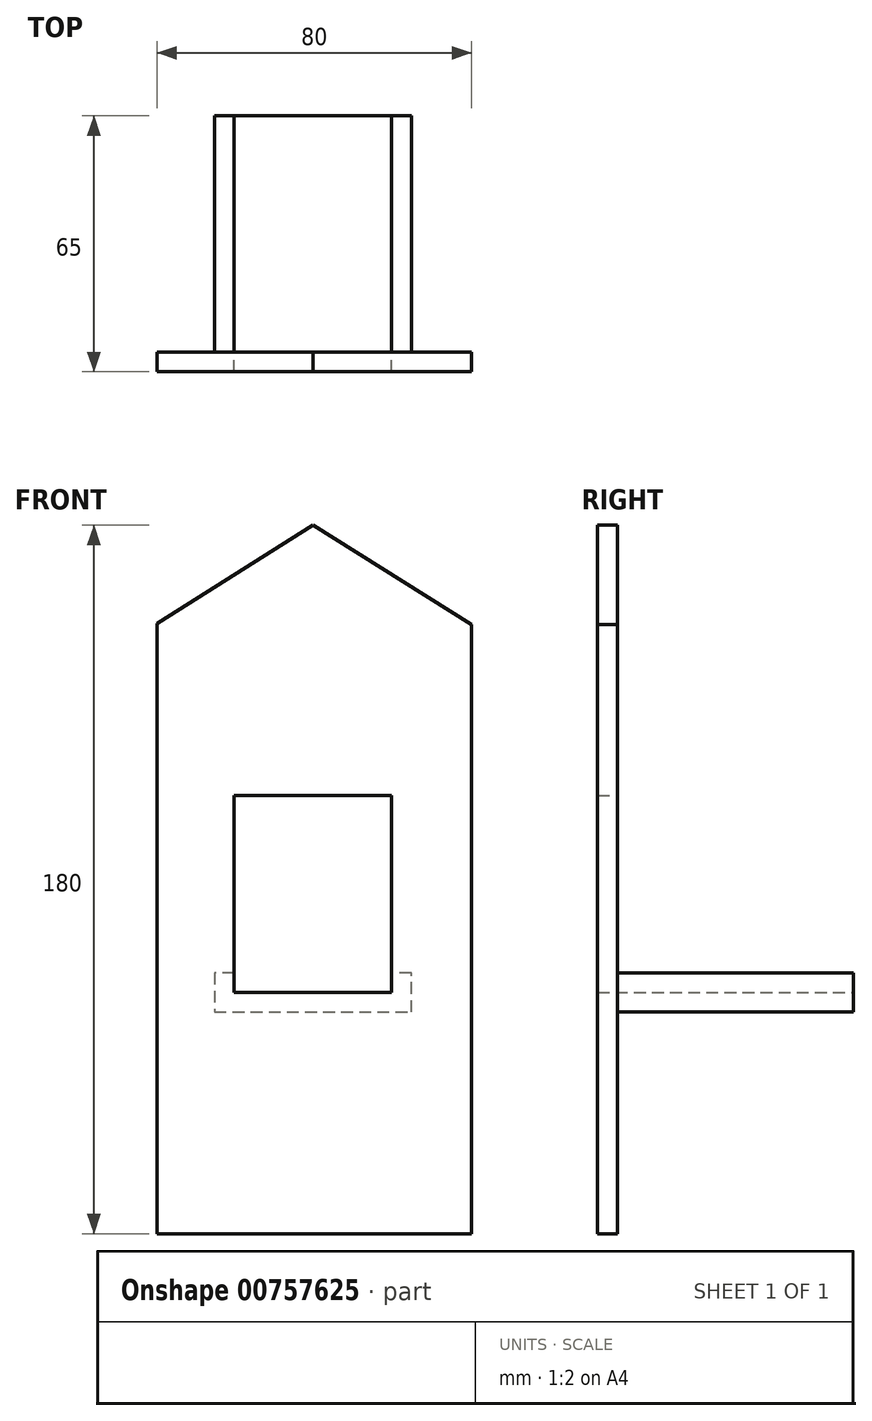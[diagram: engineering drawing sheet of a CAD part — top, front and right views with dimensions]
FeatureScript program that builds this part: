
annotation { "Feature Type Name" : "Feature", "Feature Type Description" : "" }
export const myFeature = defineFeature(function(context is Context, id is Id, definition is map)
    precondition{}
    {
        {
            var Q0;
            Q0=qCreatedBy(makeId("Front.planeOp"),FACE);
            var sketch = newSketch(context, id + "F0", { "sketchPlane" : qUnion([Q0])});
            skLineSegment(sketch, "E0.top", {"start": v(-39.65, -121.3) * mm, "end": v(40.35, -121.3) * mm});
            skLineSegment(sketch, "E0.left", {"start": v(-39.65, 33.77) * mm, "end": v(-39.65, -121.3) * mm});
            skLineSegment(sketch, "E0.right", {"start": v(40.35, 33.42) * mm, "end": v(40.35, -121.3) * mm});
            skLineSegment(sketch, "E1", {"start": v(-39.65, 33.77) * mm, "end": v(0, 58.7) * mm});
            skLineSegment(sketch, "E2", {"start": v(0, 58.7) * mm, "end": v(40.35, 33.42) * mm});
            skLineSegment(sketch, "E3.bottom", {"start": v(-20, -10) * mm, "end": v(20, -10) * mm});
            skLineSegment(sketch, "E3.top", {"start": v(-20, -60) * mm, "end": v(20, -60) * mm});
            skLineSegment(sketch, "E3.left", {"start": v(-20, -10) * mm, "end": v(-20, -60) * mm});
            skLineSegment(sketch, "E3.right", {"start": v(20, -10) * mm, "end": v(20, -60) * mm});
            skSolve(sketch);
        }
        {
            var Q0;
            Q0=makeQuery(id+"F0.imprint","IMPRINT",FACE,{"disambiguationData":[TD([[makeQuery(id+"F0.imprint","IMPRINT",EDGE,{"derivedFrom":sQuery(id+"F0.wireOp",EDGE,"E0.top")}),1.0]])]});
            extrude(context, id + "F1", {"entities" : qUnion([Q0]), "depth" : 5 * mm, "offsetDistance" : 25 * mm});
        }
        {
            var Q0;
            Q0=qCreatedBy(makeId("Front.planeOp"),FACE);
            var sketch = newSketch(context, id + "F2", { "sketchPlane" : qUnion([Q0])});
            skLineSegment(sketch, "E4", {"start": v(-25, -65) * mm, "end": v(25, -65) * mm});
            skLineSegment(sketch, "E5", {"start": v(25, -65) * mm, "end": v(25, -55) * mm});
            skLineSegment(sketch, "E6", {"start": v(25, -55) * mm, "end": v(20, -55) * mm});
            skLineSegment(sketch, "E7", {"start": v(20, -55) * mm, "end": v(20, -60) * mm});
            skLineSegment(sketch, "E8", {"start": v(20, -60) * mm, "end": v(-20, -60) * mm});
            skLineSegment(sketch, "E9", {"start": v(-20, -60) * mm, "end": v(-20, -55) * mm});
            skLineSegment(sketch, "E10", {"start": v(-20, -55) * mm, "end": v(-25, -55) * mm});
            skLineSegment(sketch, "E11", {"start": v(-25, -55) * mm, "end": v(-25, -65) * mm});
            skSolve(sketch);
        }
        {
            var Q0;
            Q0 = qSketchRegion(id + "F2", true);
            extrude(context, id + "F3", {"entities" : qUnion([Q0]), "operationType" : NewBodyOperationType.ADD, "oppositeDirection" : true, "depth" : 60 * mm, "offsetDistance" : 25 * mm});
        }
    });
